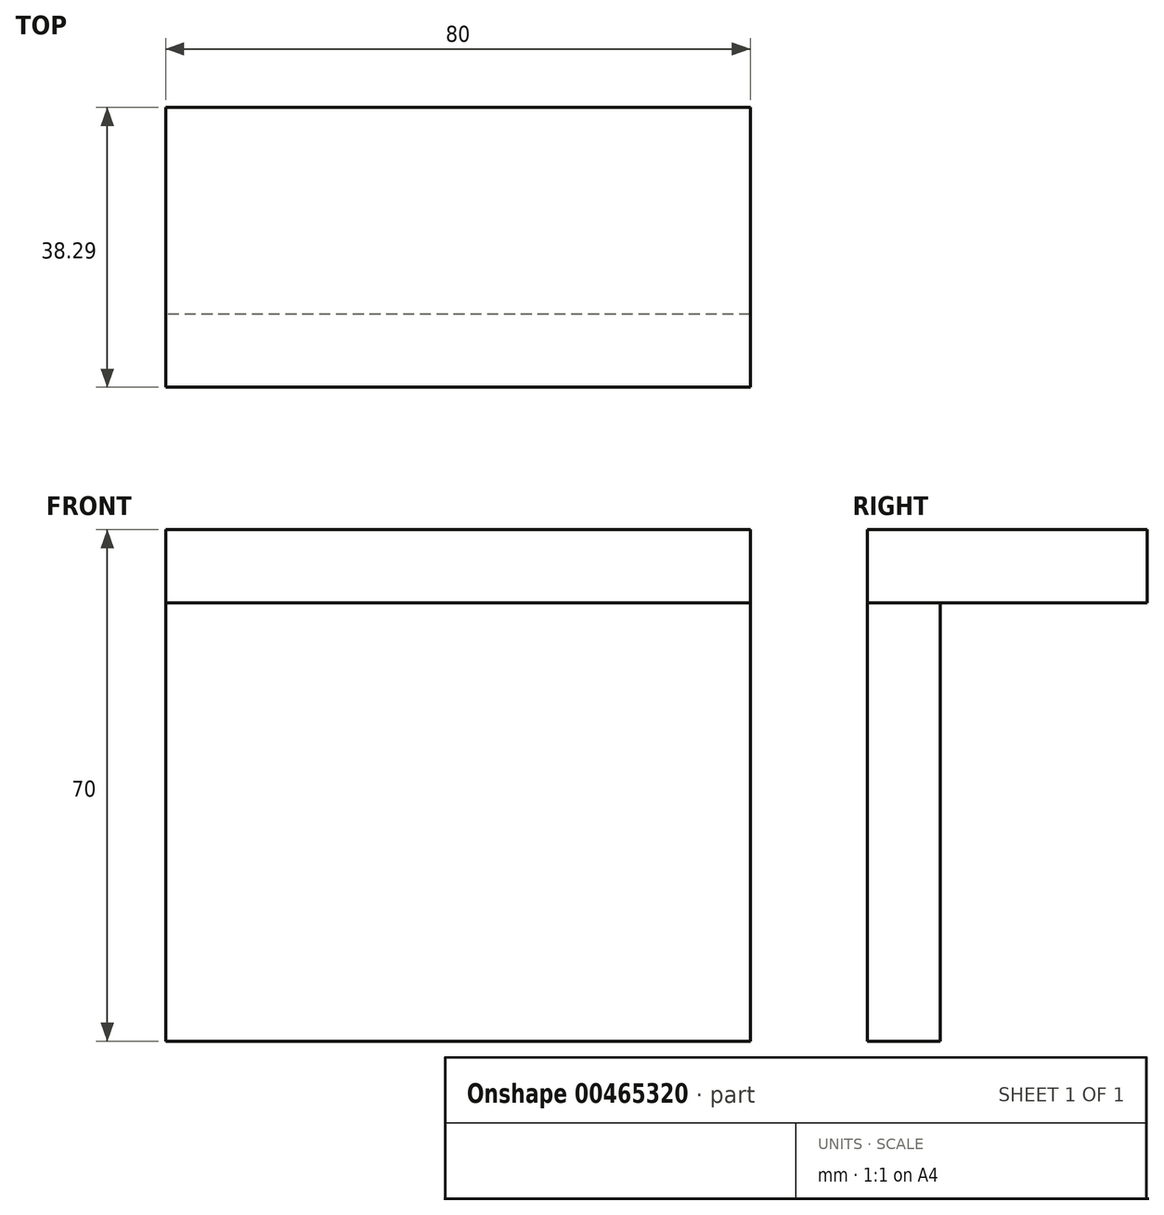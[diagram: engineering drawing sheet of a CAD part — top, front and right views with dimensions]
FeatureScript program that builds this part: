
annotation { "Feature Type Name" : "Feature", "Feature Type Description" : "" }
export const myFeature = defineFeature(function(context is Context, id is Id, definition is map)
    precondition{}
    {
        {
            var Q0;
            Q0=qCreatedBy(makeId("Right.planeOp"),FACE);
            var sketch = newSketch(context, id + "F0", { "sketchPlane" : qUnion([Q0])});
            skLineSegment(sketch, "E0.bottom", {"start": v(-3.7, -28.87) * mm, "end": v(6.3, -28.87) * mm});
            skLineSegment(sketch, "E0.top", {"start": v(-3.7, 31.13) * mm, "end": v(6.3, 31.13) * mm});
            skLineSegment(sketch, "E0.left", {"start": v(-3.7, -28.87) * mm, "end": v(-3.7, 31.13) * mm});
            skLineSegment(sketch, "E0.right", {"start": v(6.3, -28.87) * mm, "end": v(6.3, 31.13) * mm});
            skSolve(sketch);
        }
        {
            var Q0;
            Q0 = qSketchRegion(id + "F0", true);
            extrude(context, id + "F1", {"entities" : qUnion([Q0]), "depth" : 40 * mm, "hasSecondDirection" : true, "secondDirectionOppositeDirection" : true, "secondDirectionDepth" : 40 * mm});
        }
        {
            var Q0;
            Q0=qCreatedBy(makeId("Right.planeOp"),FACE);
            var sketch = newSketch(context, id + "F2", { "sketchPlane" : qUnion([Q0])});
            skLineSegment(sketch, "E1.bottom", {"start": v(34.59, 41.13) * mm, "end": v(-3.7, 41.13) * mm});
            skLineSegment(sketch, "E1.top", {"start": v(34.59, 31.13) * mm, "end": v(-3.7, 31.13) * mm});
            skLineSegment(sketch, "E1.left", {"start": v(34.59, 41.13) * mm, "end": v(34.59, 31.13) * mm});
            skLineSegment(sketch, "E1.right", {"start": v(-3.7, 41.13) * mm, "end": v(-3.7, 31.13) * mm});
            skSolve(sketch);
        }
        {
            var Q0;
            Q0 = qSketchRegion(id + "F2", true);
            var Q1;
            Q1=makeQuery(id+"F1.opExtrude","CAP_FACE",FACE,{"disambiguationData":[OSD([sQuery(id+"F0.wireOp",EDGE,"E0.bottom"),sQuery(id+"F0.wireOp",EDGE,"E0.top"),sQuery(id+"F0.wireOp",EDGE,"E0.left"),sQuery(id+"F0.wireOp",EDGE,"E0.right")])],"isStart":false});
            var Q2;
            Q2=makeQuery(id+"F1.opExtrude","CAP_FACE",FACE,{"disambiguationData":[OSD([sQuery(id+"F0.wireOp",EDGE,"E0.bottom"),sQuery(id+"F0.wireOp",EDGE,"E0.top"),sQuery(id+"F0.wireOp",EDGE,"E0.left"),sQuery(id+"F0.wireOp",EDGE,"E0.right")])],"isStart":true});
            extrude(context, id + "F3", {"entities" : qUnion([Q0]), "endBound" : BoundingType.UP_TO_SURFACE, "endBoundEntityFace" : qUnion([Q1]), "depth" : 25 * mm, "hasSecondDirection" : true, "secondDirectionBound" : SecondDirectionBoundingType.UP_TO_SURFACE, "secondDirectionOppositeDirection" : true, "secondDirectionBoundEntityFace" : qUnion([Q2]), "secondDirectionDepth" : 25 * mm});
        }
    });
